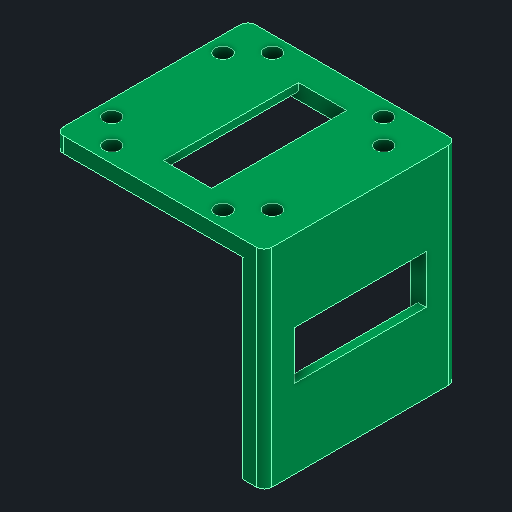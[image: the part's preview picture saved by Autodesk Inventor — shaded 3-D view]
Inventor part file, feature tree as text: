
AUTODESK INVENTOR PART (.ipt)
format: ipt  version: 2023.4 (Build 274418000, 418)  size: 285,184 bytes
history: native  units: mm
features: extrude x7, sketch x4, other x4, reference x2, projected_geometry x2, plane x1, fillet x1, chamfer x1
ambient origin geometry x8: Origin, YZ Plane, XZ Plane, XY Plane, X Axis, Y Axis, Z Axis, Center Point
bodies: Solid1 (feature_tree)
feature tree (22):
  sketch  "Sketch1"  dims[d0=4.0mm d1=0.0mm d2=2.5mm]
  plane  "Work Plane1"
  extrude  "Extrusion1"  Depth=4.0mm
  sketch  "Sketch2"  dims[d3=6.25mm d4=4.125mm]
  extrude  "Extrusion2"  Depth=4.125mm
  extrude  "Extrusion3"  Depth=2.0mm TaperAngle=0.0deg
  extrude  "Extrusion4"  Depth=2.0mm
  extrude  "Extrusion5"  Depth=2.0mm
  fillet  "Fillet1"  Radius=49.8mm
  extrude  "Extrusion6"  Depth=2.0mm
  extrude  "Extrusion7"  Depth=7.5mm
  chamfer  "Chamfer1"  Distance=7.5mm
  reference  "Reference1"
  projected_geometry  "Projected Loop1"
  sketch  "Sketch3"  dims[d5=2.0mm d6=0.0mm d7=2.0mm d8=0.0mm]
  reference  "Reference2"
  sketch  "Sketch4"  dims[d9=49.8mm d10=0.0mm d11=2.0mm d12=2.5mm d13=49.8mm d14=0.0mm d15=0.125mm d16=7.5mm d17=7.5mm d18=2.0mm d19=0.0mm d20=7.5mm d21=7.5mm d22=2.0mm d23=0.0mm d24=2.0mm d25=2.0mm d26=45.0deg]
  projected_geometry  "Projected Loop2"
  other  "<path>\Projects\Project Protocube\Protocube\CAD, STL, OBJ Files\1 CAD\Cube 1x1 V5.iam"
  other  "Cube 1x1 V5.iam"
  other  "Cube 1x1 Top V5 Closed Slotted:1"
  other  "Cube 1x1 Bottom V5 Closed Slotted:1"
note: 1 file-system path scrubbed to <path> (originals preserved in map.json)
